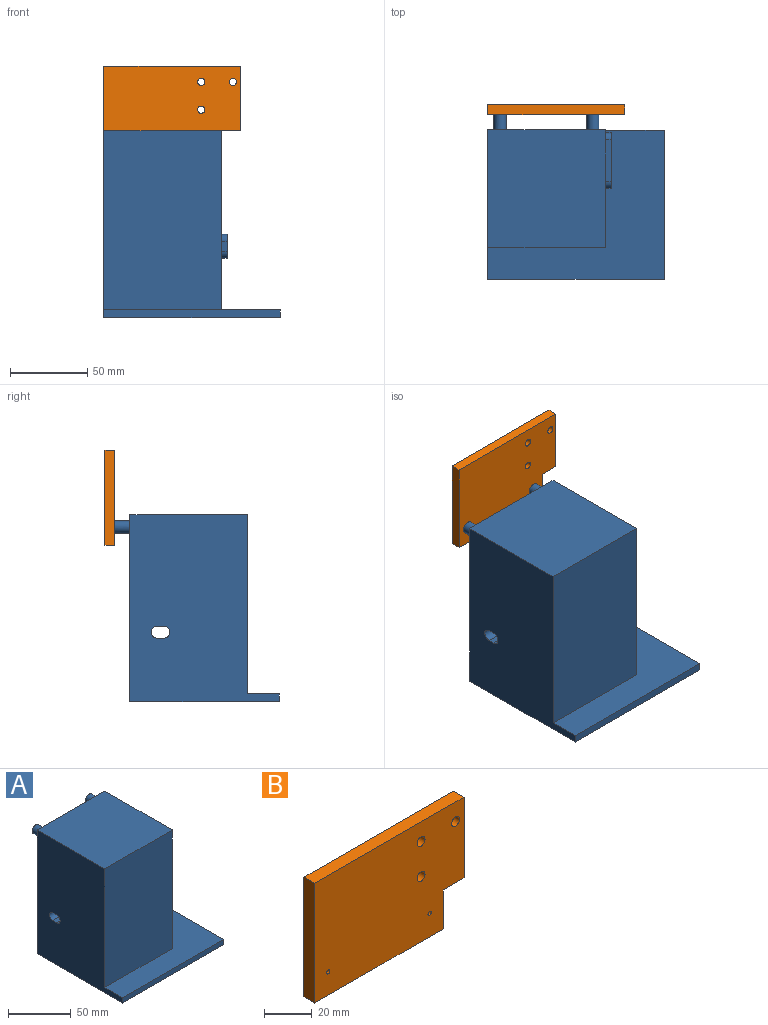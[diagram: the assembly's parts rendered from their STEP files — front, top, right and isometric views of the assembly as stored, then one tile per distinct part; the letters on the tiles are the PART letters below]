
ASSEMBLY  parts=2 mates=1
PART A: 35 faces, bbox 114.2x106.3x121 mm
  f0: plane 114.2x5mm, normal (0,-1,0), area 571mm2, adj f1,f4,f5,f8
  f1: plane 96.5x5mm, normal (1,0,0), area 482.5mm2, adj f0,f3,f5,f8
  f2: plane 76.2x76.2mm, normal (0,0,1), area 5806.4mm2, adj f3,f4,f6,f7
  f3: plane 121x114.2mm, normal (0,1,0), area 9309.7mm2, adj f1,f2,f4,f5,f7,f8,f31,f33
  f4: plane 121x96.5mm, normal (-1,0,0), area 9241.2mm2, adj f0,f2,f3,f5,f6,f8,f27,f28
  f5: plane 114.2x96.5mm, normal (0,0,-1), area 11020.3mm2, adj f0,f1,f3,f4
  f6: plane 116x76.2mm, normal (0,-1,0), area 8839.2mm2, adj f2,f4,f7,f8
  f7: plane 116x76.2mm, normal (1,0,0), area 8300mm2, adj f2,f3,f6,f8,f9,f10,f11,f12
  f8: plane 114.2x96.5mm, normal (0,0,1), area 5213.9mm2, adj f0,f1,f3,f4,f6,f7
  f9: plane 27x3.65mm, normal (0,0,1), area 98.6mm2, adj f7,f13,f14,f17
  f10: plane 6.46x3.65mm, normal (0,-1,0), area 23.6mm2, adj f7,f13,f14,f15
  f11: plane 27x3.65mm, normal (0,0,-1), area 98.6mm2, adj f7,f13,f15,f16
  f12: plane 6.46x3.65mm, normal (0,1,0), area 23.6mm2, adj f7,f13,f16,f17
  f13: plane 36x15.46mm, normal (1,0,0), area 160.3mm2, adj f9,f10,f11,f12,f14,f15,f16,f17
  f14: cylinder r=4.5mm len=4.5mm, axis (1,0,0), area 25.8mm2, adj f7,f9,f10,f13
  f15: cylinder r=4.5mm len=4.5mm, axis (-1,0,0), area 25.8mm2, adj f7,f10,f11,f13
  f16: cylinder r=4.5mm len=4.5mm, axis (1,0,0), area 25.8mm2, adj f7,f11,f12,f13
  f17: cylinder r=4.5mm len=4.5mm, axis (-1,0,0), area 25.8mm2, adj f7,f9,f12,f13
  f18: cylinder r=2.5mm len=3.6mm, axis (1,0,0), area 14.1mm2, adj f13,f19,f25,f26
  f19: plane 6.86x3.6mm, normal (0,1,0), area 24.7mm2, adj f13,f18,f20,f26
  f20: cylinder r=2.5mm len=3.6mm, axis (1,0,0), area 14.1mm2, adj f13,f19,f21,f26
  f21: plane 27.4x3.6mm, normal (0,0,1), area 98.6mm2, adj f13,f20,f22,f26
  f22: cylinder r=2.5mm len=3.6mm, axis (1,0,0), area 14.1mm2, adj f13,f21,f23,f26
  f23: plane 6.86x3.6mm, normal (0,-1,0), area 24.7mm2, adj f13,f22,f24,f26
  f24: cylinder r=2.5mm len=3.6mm, axis (1,0,0), area 14.1mm2, adj f13,f23,f25,f26
  f25: plane 27.4x3.6mm, normal (0,0,-1), area 98.6mm2, adj f13,f18,f24,f26
  f26: plane 32.4x11.86mm, normal (1,0,0), area 298.4mm2, adj f18,f19,f20,f21,f22,f23,f24,f25
  f27: plane 76.25x4.2mm, normal (0,0,-1), area 320.2mm2, adj f4,f26,f28,f30
  f28: cylinder r=3.9mm len=76.25mm, axis (1,0,0), area 934.2mm2, adj f4,f26,f27,f29
  f29: plane 76.25x4.2mm, normal (0,0,1), area 320.2mm2, adj f4,f26,f28,f30
  f30: cylinder r=3.9mm len=76.25mm, axis (1,0,0), area 934.2mm2, adj f4,f26,f27,f29
  f31: cylinder r=4mm len=9.8mm, axis (0,-1,0), area 246.3mm2, adj f3,f32
  f32: plane 8x8mm, normal (0,1,0), area 50.3mm2, adj f31
  f33: cylinder r=4mm len=9.8mm, axis (0,-1,0), area 246.3mm2, adj f3,f34
  f34: plane 8x8mm, normal (0,1,0), area 50.3mm2, adj f33
PART B: 13 faces, bbox 88.6x6.4x61.5 mm
  f0: plane 88.6x6.4mm, normal (0,0,1), area 567mm2, adj f1,f5,f6,f7
  f1: plane 61.5x6.4mm, normal (-1,0,0), area 393.6mm2, adj f0,f2,f6,f7
  f2: plane 76.2x6.4mm, normal (0,0,-1), area 487.7mm2, adj f1,f3,f6,f7
  f3: plane 20x6.4mm, normal (1,0,0), area 128mm2, adj f2,f4,f6,f7
  f4: plane 12.4x6.4mm, normal (0,0,-1), area 79.4mm2, adj f3,f5,f6,f7
  f5: plane 41.5x6.4mm, normal (1,0,0), area 265.6mm2, adj f0,f4,f6,f7
  f6: plane 88.6x61.5mm, normal (0,-1,0), area 5142.6mm2, adj f0,f1,f2,f3,f4,f5,f8,f9
  f7: plane 88.6x61.5mm, normal (0,1,0), area 5142.6mm2, adj f0,f1,f2,f3,f4,f5,f8,f9
  f8: cylinder r=2.35mm len=6.4mm, axis (0,-1,0), area 94.5mm2, adj f6,f7
  f9: cylinder r=2.35mm len=6.4mm, axis (0,-1,0), area 94.5mm2, adj f6,f7
  f10: cylinder r=2.35mm len=6.4mm, axis (0,-1,0), area 94.5mm2, adj f6,f7
  f11: cylinder r=1mm len=6.4mm, axis (0,-1,0), area 40.2mm2, adj f6,f7
  f12: cylinder r=1mm len=6.4mm, axis (0,-1,0), area 40.2mm2, adj f6,f7
PLACE A t=(0.02,-4.66,-60.17)mm
PLACE B t=(19.12,59.79,60.83)mm
MATE fastened B.f11 <-> A.f31  axis (0,-1,0) through (11.12,53.39,52.83)mm
